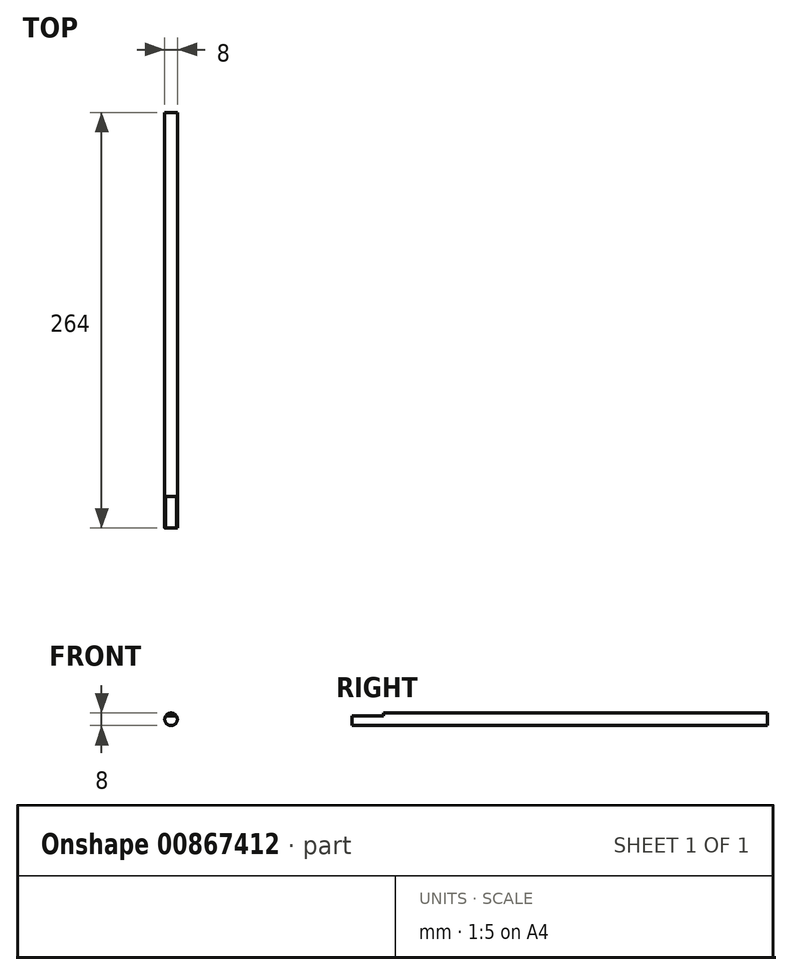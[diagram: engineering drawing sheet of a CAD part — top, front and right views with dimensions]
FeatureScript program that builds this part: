
annotation { "Feature Type Name" : "Feature", "Feature Type Description" : "" }
export const myFeature = defineFeature(function(context is Context, id is Id, definition is map)
    precondition{}
    {
        {
            var Q0;
            Q0=qCreatedBy(makeId("Front.planeOp"),FACE);
            var sketch = newSketch(context, id + "F0", { "sketchPlane" : qUnion([Q0])});
            skCircle(sketch, "E0", {"center": v(0, 0) * mm, "radius": 4 * mm});
            skSolve(sketch);
        }
        {
            var Q0;
            Q0=qSketchRegion(id+"F0",true);
            extrude(context, id + "F1", {"entities" : qUnion([Q0]), "endBound" : BoundingType.SYMMETRIC, "depth" : 294 * mm, "offsetDistance" : 25 * mm});
        }
        {
            var Q0;
            Q0=makeQuery(id+"F1.opExtrude","CAP_FACE",FACE,{"disambiguationData":[OSD([sQuery(id+"F0.wireOp",EDGE,"E0")])],"isStart":false});
            var sketch = newSketch(context, id + "F2", { "sketchPlane" : qUnion([Q0])});
            skCircle(sketch, "E1.0", {"center": v(0, 0) * mm, "radius": 4 * mm});
            skLineSegment(sketch, "E2", {"start": v(-3.46, 2) * mm, "end": v(3.46, 2) * mm});
            skSolve(sketch);
        }
        {
            var Q0;
            {var subQ0=sQuery(id+"F2.wireOp",EDGE,"E2");Q0=makeQuery(id+"F2.imprint","IMPRINT",FACE,{"disambiguationData":[TD([[makeQuery(id+"F2.imprint","IMPRINT",EDGE,{"derivedFrom":subQ0}),1.0]])]});}
            extrude(context, id + "F3", {"entities" : qUnion([Q0]), "operationType" : NewBodyOperationType.REMOVE, "oppositeDirection" : true, "depth" : 20 * mm, "offsetDistance" : 25 * mm});
        }
        {
            var Q0;
            Q0=makeQuery(id+"F1.opExtrude","CAP_FACE",FACE,{"disambiguationData":[OSD([sQuery(id+"F0.wireOp",EDGE,"E0")])],"isStart":true});
            extrude(context, id + "F4", {"entities" : qUnion([Q0]), "operationType" : NewBodyOperationType.REMOVE, "oppositeDirection" : true, "depth" : 30 * mm, "offsetDistance" : 25 * mm});
        }
    });
